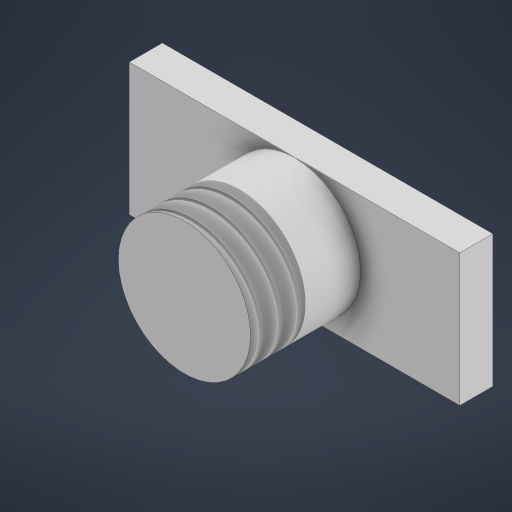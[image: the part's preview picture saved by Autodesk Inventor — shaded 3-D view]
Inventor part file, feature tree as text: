
AUTODESK INVENTOR PART (.ipt)
format: ipt  version: 2023 (Build 270158000, 158)  size: 197,120 bytes
history: native  units: mm
features: extrude x2, sketch x2, thread x1
ambient origin geometry x8: Origin, YZ Plane, XZ Plane, XY Plane, X Axis, Y Axis, Z Axis, Center Point
bodies: Solid1 (feature_tree)
feature tree (5):
  extrude  "Extrusion1"  Depth=12.0mm
  extrude  "Extrusion2"  Depth=12.0mm
  thread  "Thread2"  [1 undecoded]
  sketch  "Sketch1"  dims[d0=30.0mm d1=12.0mm]
  sketch  "Sketch2"  dims[d2=3.0mm d3=0.0mm d4=12.0mm d5=10.0mm d6=0.0mm d16=5.0mm d17=0.0mm d18=0.5mm d19=0.872665mm]
note: 1 required parameter value undecoded (feature->parameter linkage not recoverable at this tier; creation-order binding heuristic only, values carry confidence <= 0.55)
